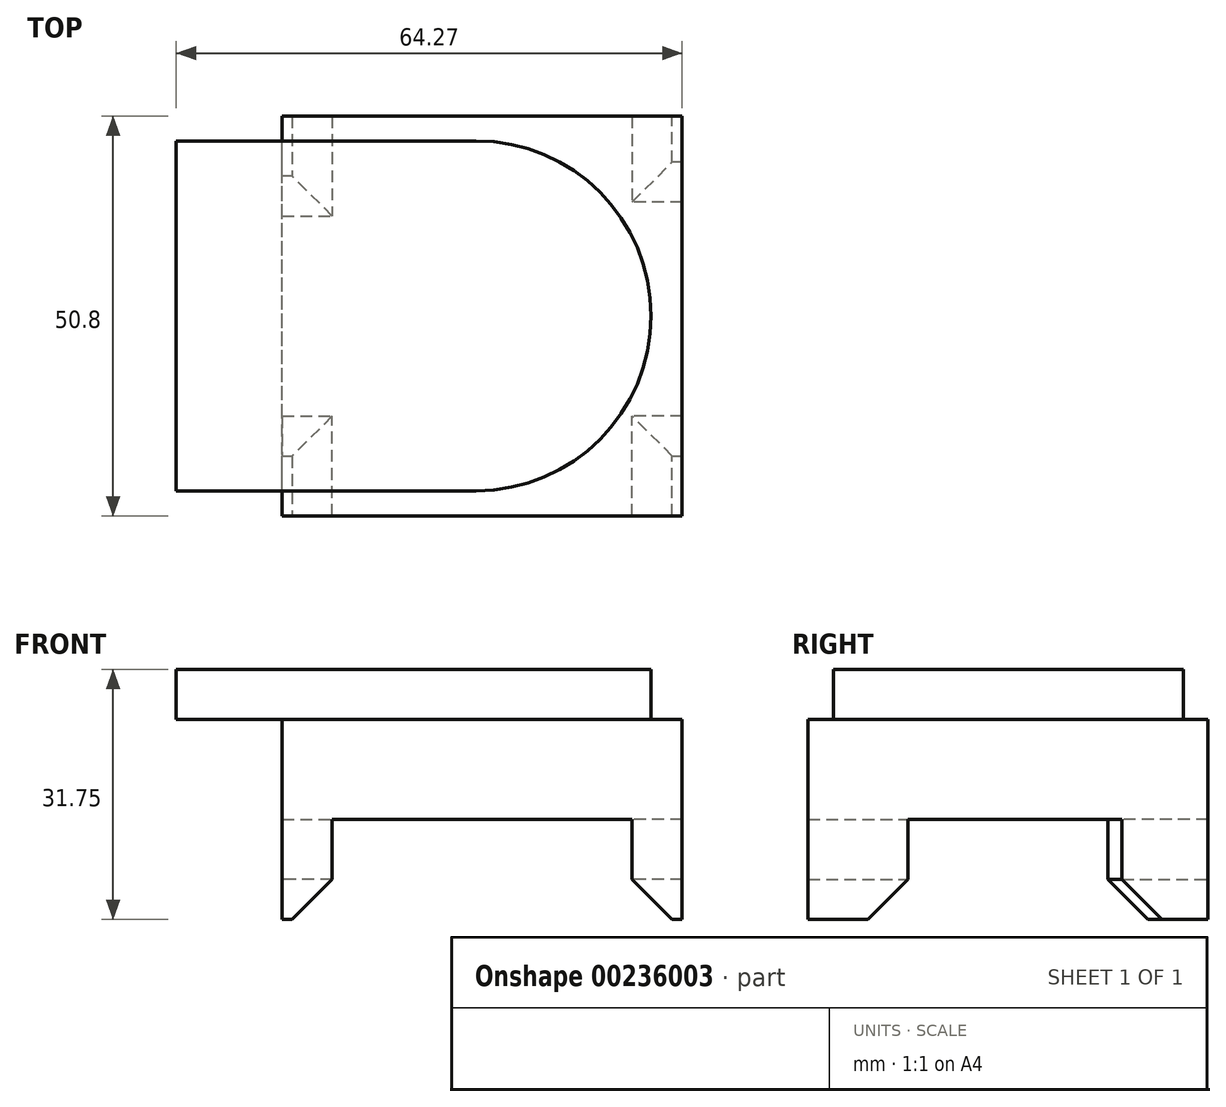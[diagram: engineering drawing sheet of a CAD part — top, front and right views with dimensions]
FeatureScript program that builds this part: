
annotation { "Feature Type Name" : "Feature", "Feature Type Description" : "" }
export const myFeature = defineFeature(function(context is Context, id is Id, definition is map)
    precondition{}
    {
        {
            var Q0;
            Q0=qCreatedBy(makeId("Top.planeOp"),FACE);
            var sketch = newSketch(context, id + "F0", { "sketchPlane" : qUnion([Q0])});
            skLineSegment(sketch, "E0.bottom", {"start": v(-24.63, -25.43) * mm, "end": v(26.17, -25.43) * mm});
            skLineSegment(sketch, "E0.top", {"start": v(-24.63, 25.37) * mm, "end": v(26.17, 25.37) * mm});
            skLineSegment(sketch, "E0.left", {"start": v(-24.63, -25.43) * mm, "end": v(-24.63, 25.37) * mm});
            skLineSegment(sketch, "E0.right", {"start": v(26.17, -25.43) * mm, "end": v(26.17, 25.37) * mm});
            skSolve(sketch);
        }
        {
            var Q0;
            Q0 = qSketchRegion(id + "F0", true);
            extrude(context, id + "F1", {"entities" : qUnion([Q0]), "oppositeDirection" : true, "depth" : 12.7 * mm});
        }
        {
            var Q0;
            Q0=makeQuery(id+"F1.opExtrude","CAP_FACE",FACE,{"disambiguationData":[OSD([sQuery(id+"F0.wireOp",EDGE,"E0.bottom"),sQuery(id+"F0.wireOp",EDGE,"E0.top"),sQuery(id+"F0.wireOp",EDGE,"E0.left"),sQuery(id+"F0.wireOp",EDGE,"E0.right")])],"isStart":false});
            var sketch = newSketch(context, id + "F2", { "sketchPlane" : qUnion([Q0])});
            skLineSegment(sketch, "E1.bottom", {"start": v(-24.63, 25.43) * mm, "end": v(-18.28, 25.43) * mm});
            skLineSegment(sketch, "E1.top", {"start": v(-24.63, 12.73) * mm, "end": v(-18.28, 12.73) * mm});
            skLineSegment(sketch, "E1.left", {"start": v(-24.63, 25.43) * mm, "end": v(-24.63, 12.73) * mm});
            skLineSegment(sketch, "E1.right", {"start": v(-18.28, 25.43) * mm, "end": v(-18.28, 12.73) * mm});
            skLineSegment(sketch, "E2.bottom", {"start": v(26.17, 25.43) * mm, "end": v(19.82, 25.43) * mm});
            skLineSegment(sketch, "E2.top", {"start": v(26.17, 12.73) * mm, "end": v(19.82, 12.73) * mm});
            skLineSegment(sketch, "E2.left", {"start": v(26.17, 25.43) * mm, "end": v(26.17, 12.73) * mm});
            skLineSegment(sketch, "E2.right", {"start": v(19.82, 25.43) * mm, "end": v(19.82, 12.73) * mm});
            skLineSegment(sketch, "E3.bottom", {"start": v(-24.63, -25.37) * mm, "end": v(-18.28, -25.37) * mm});
            skLineSegment(sketch, "E3.top", {"start": v(-24.63, -12.67) * mm, "end": v(-18.28, -12.67) * mm});
            skLineSegment(sketch, "E3.left", {"start": v(-24.63, -25.37) * mm, "end": v(-24.63, -12.67) * mm});
            skLineSegment(sketch, "E3.right", {"start": v(-18.28, -25.37) * mm, "end": v(-18.28, -12.67) * mm});
            skLineSegment(sketch, "E4.bottom", {"start": v(26.17, -25.37) * mm, "end": v(19.82, -25.37) * mm});
            skLineSegment(sketch, "E4.top", {"start": v(26.17, -14.44) * mm, "end": v(19.82, -14.44) * mm});
            skLineSegment(sketch, "E4.left", {"start": v(26.17, -25.37) * mm, "end": v(26.17, -14.44) * mm});
            skLineSegment(sketch, "E4.right", {"start": v(19.82, -25.37) * mm, "end": v(19.82, -14.44) * mm});
            skSolve(sketch);
        }
        {
            var Q0;
            Q0 = qSketchRegion(id + "F2", true);
            extrude(context, id + "F3", {"entities" : qUnion([Q0]), "operationType" : NewBodyOperationType.ADD, "depth" : 12.7 * mm});
        }
        {
            var Q0;
            Q0=makeQuery(id+"F3.opExtrude","CAP_EDGE",EDGE,{"disambiguationData":[OSD([sQuery(id+"F2.wireOp",EDGE,"E1.top")])],"isStart":false});
            var Q1;
            Q1=makeQuery(id+"F3.opExtrude","CAP_EDGE",EDGE,{"disambiguationData":[OSD([sQuery(id+"F2.wireOp",EDGE,"E1.right")])],"isStart":false});
            var Q2;
            Q2=makeQuery(id+"F3.opExtrude","CAP_EDGE",EDGE,{"disambiguationData":[OSD([sQuery(id+"F2.wireOp",EDGE,"E2.right")])],"isStart":false});
            var Q3;
            Q3=makeQuery(id+"F3.opExtrude","CAP_EDGE",EDGE,{"disambiguationData":[OSD([sQuery(id+"F2.wireOp",EDGE,"E2.top")])],"isStart":false});
            var Q4;
            Q4=makeQuery(id+"F3.opExtrude","CAP_EDGE",EDGE,{"disambiguationData":[OSD([sQuery(id+"F2.wireOp",EDGE,"E3.right")])],"isStart":false});
            var Q5;
            Q5=makeQuery(id+"F3.opExtrude","CAP_EDGE",EDGE,{"disambiguationData":[OSD([sQuery(id+"F2.wireOp",EDGE,"E3.top")])],"isStart":false});
            var Q6;
            Q6=makeQuery(id+"F3.opExtrude","CAP_EDGE",EDGE,{"disambiguationData":[OSD([sQuery(id+"F2.wireOp",EDGE,"E4.top")])],"isStart":false});
            var Q7;
            Q7=makeQuery(id+"F3.opExtrude","CAP_EDGE",EDGE,{"disambiguationData":[OSD([sQuery(id+"F2.wireOp",EDGE,"E4.right")])],"isStart":false});
            chamfer(context, id + "F4", {"entities" : qUnion([Q0, Q1, Q2, Q3, Q4, Q5, Q6, Q7]), "width" : 5.08 * mm, "tangentPropagation" : true});
        }
        {
            var Q0;
            Q0=makeQuery(id+"F1.opExtrude","CAP_FACE",FACE,{"disambiguationData":[OSD([sQuery(id+"F0.wireOp",EDGE,"E0.bottom"),sQuery(id+"F0.wireOp",EDGE,"E0.top"),sQuery(id+"F0.wireOp",EDGE,"E0.left"),sQuery(id+"F0.wireOp",EDGE,"E0.right")])],"isStart":true});
            var sketch = newSketch(context, id + "F5", { "sketchPlane" : qUnion([Q0])});
            skCircle(sketch, "E5", {"center": v(0, 0) * mm, "radius": 22.23 * mm});
            skSolve(sketch);
        }
        {
            var Q0;
            Q0=makeQuery(id+"F5.imprint","IMPRINT",FACE,{"disambiguationData":[TD([[makeQuery(id+"F5.imprint","IMPRINT",EDGE,{"derivedFrom":sQuery(id+"F5.wireOp",EDGE,"E5")}),1.0]])]});
            extrude(context, id + "F6", {"entities" : qUnion([Q0]), "operationType" : NewBodyOperationType.ADD, "depth" : 6.35 * mm});
        }
        {
            var Q0;
            Q0=makeQuery(id+"F1.opExtrude","CAP_FACE",FACE,{"disambiguationData":[OSD([sQuery(id+"F0.wireOp",EDGE,"E0.bottom"),sQuery(id+"F0.wireOp",EDGE,"E0.top"),sQuery(id+"F0.wireOp",EDGE,"E0.left"),sQuery(id+"F0.wireOp",EDGE,"E0.right")])],"isStart":true});
            var sketch = newSketch(context, id + "F7", { "sketchPlane" : qUnion([Q0])});
            skLineSegment(sketch, "E6.bottom", {"start": v(0, -22.23) * mm, "end": v(-38.1, -22.23) * mm});
            skLineSegment(sketch, "E6.top", {"start": v(0, 22.23) * mm, "end": v(-38.1, 22.22) * mm});
            skLineSegment(sketch, "E6.left", {"start": v(0, -22.23) * mm, "end": v(0, 22.23) * mm});
            skLineSegment(sketch, "E6.right", {"start": v(-38.1, -22.23) * mm, "end": v(-38.1, 22.22) * mm});
            skSolve(sketch);
        }
        {
            var Q0;
            Q0 = qSketchRegion(id + "F7", true);
            extrude(context, id + "F8", {"entities" : qUnion([Q0]), "operationType" : NewBodyOperationType.ADD, "depth" : 6.35 * mm});
        }
    });
